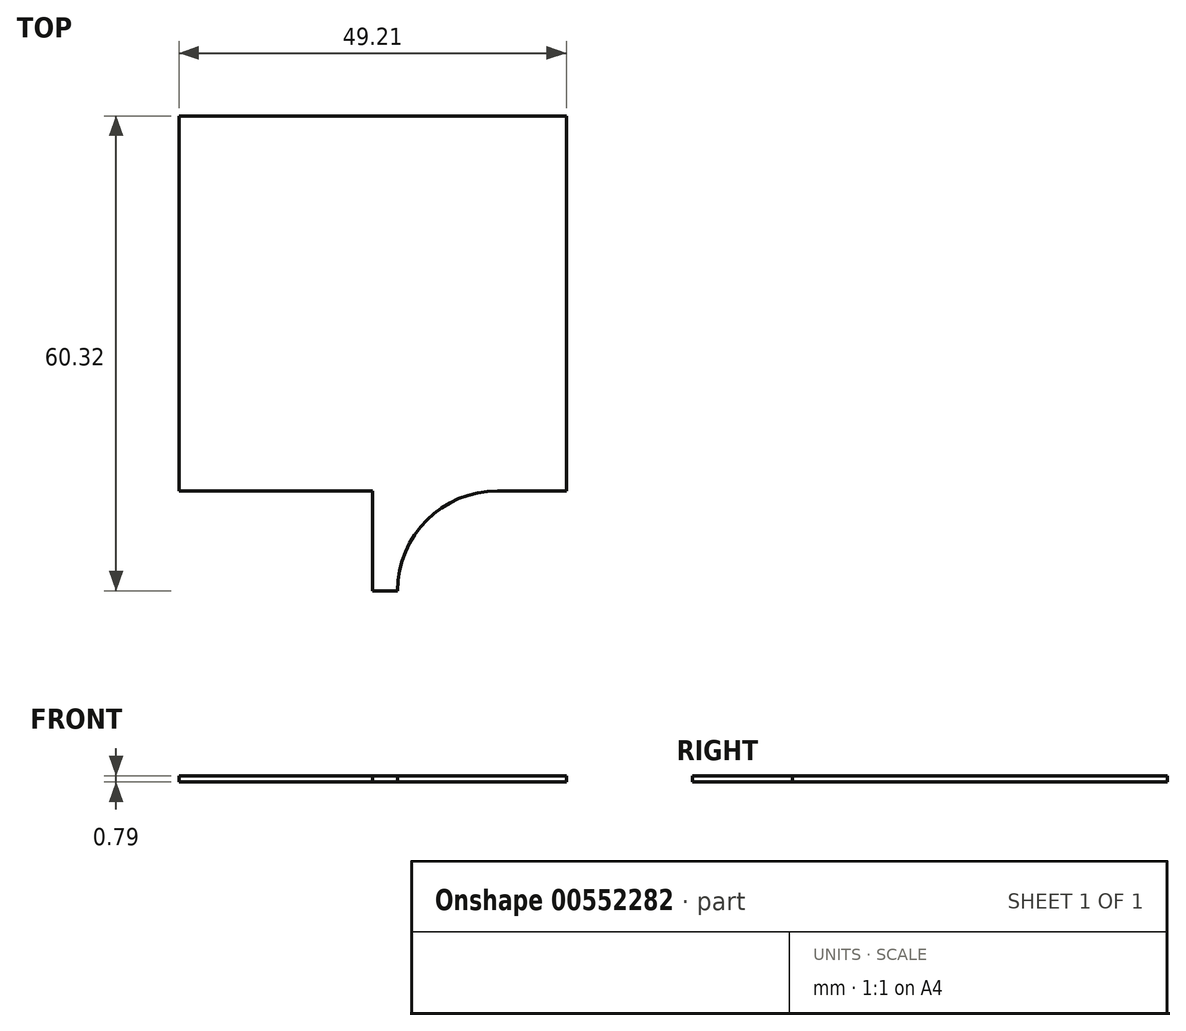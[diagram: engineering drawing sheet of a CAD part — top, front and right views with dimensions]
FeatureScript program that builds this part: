
annotation { "Feature Type Name" : "Feature", "Feature Type Description" : "" }
export const myFeature = defineFeature(function(context is Context, id is Id, definition is map)
    precondition{}
    {
        {
            var Q0;
            Q0=qCreatedBy(makeId("Top.planeOp"),FACE);
            var sketch = newSketch(context, id + "F0", { "sketchPlane" : qUnion([Q0])});
            skLineSegment(sketch, "E0.bottom", {"start": v(-60.65, -18.77) * mm, "end": v(-11.44, -18.77) * mm});
            skLineSegment(sketch, "E0.top", {"start": v(-60.65, -66.4) * mm, "end": v(-11.44, -66.4) * mm});
            skLineSegment(sketch, "E0.left", {"start": v(-60.65, -18.77) * mm, "end": v(-60.65, -66.4) * mm});
            skLineSegment(sketch, "E0.right", {"start": v(-11.44, -18.77) * mm, "end": v(-11.44, -66.4) * mm});
            skSolve(sketch);
        }
        {
            var Q0;
            Q0=makeQuery(id+"F0.imprint","IMPRINT",FACE,{"disambiguationData":[TD([[makeQuery(id+"F0.imprint","IMPRINT",EDGE,{"derivedFrom":sQuery(id+"F0.wireOp",EDGE,"E0.bottom")}),-1.0]])]});
            extrude(context, id + "F1", {"entities" : qUnion([Q0]), "depth" : 0.8 * mm, "offsetDistance" : 25.4 * mm});
        }
        {
            var Q0;
            Q0=makeQuery(id+"F1.opExtrude","CAP_FACE",FACE,{"disambiguationData":[OSD([sQuery(id+"F0.wireOp",EDGE,"E0.bottom"),sQuery(id+"F0.wireOp",EDGE,"E0.top"),sQuery(id+"F0.wireOp",EDGE,"E0.left"),sQuery(id+"F0.wireOp",EDGE,"E0.right")])],"isStart":false});
            var sketch = newSketch(context, id + "F2", { "sketchPlane" : qUnion([Q0])});
            skLineSegment(sketch, "E1.bottom", {"start": v(-36.05, -66.4) * mm, "end": v(-32.87, -66.4) * mm});
            skLineSegment(sketch, "E1.top", {"start": v(-36.05, -79.1) * mm, "end": v(-32.87, -79.1) * mm});
            skLineSegment(sketch, "E1.left", {"start": v(-36.05, -66.4) * mm, "end": v(-36.05, -79.1) * mm});
            skLineSegment(sketch, "E1.right", {"start": v(-32.87, -66.4) * mm, "end": v(-32.87, -79.1) * mm});
            skSolve(sketch);
        }
        {
            var Q0;
            Q0 = qSketchRegion(id + "F2", true);
            extrude(context, id + "F3", {"entities" : qUnion([Q0]), "operationType" : NewBodyOperationType.ADD, "oppositeDirection" : true, "depth" : 0.8 * mm, "offsetDistance" : 25.4 * mm});
        }
        {
            var Q0;
            Q0=makeQuery(id+"F3.opExtrude","SWEPT_EDGE",EDGE,{"disambiguationData":[OSD([sQuery(id+"F0.wireOp",EDGE,"E0.top"),sQuery(id+"F2.wireOp",EDGE,"E1.bottom"),sQuery(id+"F2.wireOp",EDGE,"E1.left")])]});
            var Q1;
            Q1=makeQuery(id+"F3.opExtrude","SWEPT_EDGE",EDGE,{"disambiguationData":[OSD([sQuery(id+"F0.wireOp",EDGE,"E0.top"),sQuery(id+"F2.wireOp",EDGE,"E1.bottom"),sQuery(id+"F2.wireOp",EDGE,"E1.right")])]});
            fillet(context, id + "F4", {"entities" : qUnion([Q0, Q1]), "radius" : 12.7 * mm, "tangentPropagation" : true, "allowEdgeOverflow" : false});
        }
    });
